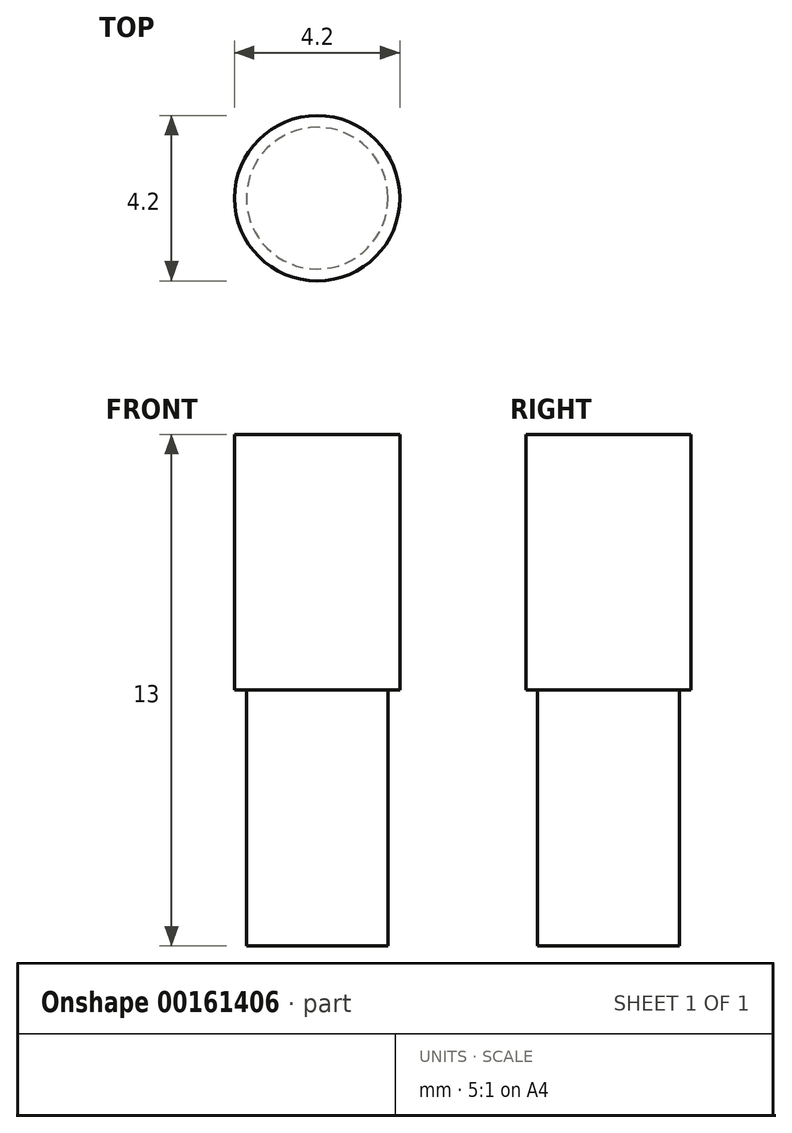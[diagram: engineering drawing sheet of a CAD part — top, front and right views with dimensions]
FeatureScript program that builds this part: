
annotation { "Feature Type Name" : "Feature", "Feature Type Description" : "" }
export const myFeature = defineFeature(function(context is Context, id is Id, definition is map)
    precondition{}
    {
        {
            var Q0;
            Q0=qCreatedBy(makeId("Top.planeOp"),FACE);
            var sketch = newSketch(context, id + "F0", { "sketchPlane" : qUnion([Q0])});
            skCircle(sketch, "E0", {"center": v(0, 0) * mm, "radius": 2.1 * mm});
            skSolve(sketch);
        }
        {
            var Q0;
            Q0=qSketchRegion(id+"F0",true);
            extrude(context, id + "F1", {"entities" : qUnion([Q0]), "oppositeDirection" : true, "depth" : 6.5 * mm});
        }
        {
            var Q0;
            Q0=makeQuery(id+"F1.opExtrude","CAP_FACE",FACE,{"disambiguationData":[OSD([sQuery(id+"F0.wireOp",EDGE,"E0")])],"isStart":false});
            var sketch = newSketch(context, id + "F2", { "sketchPlane" : qUnion([Q0])});
            skCircle(sketch, "E1", {"center": v(0, 0) * mm, "radius": 1.8 * mm});
            skSolve(sketch);
        }
        {
            var Q0;
            Q0=qSketchRegion(id+"F2",true);
            extrude(context, id + "F3", {"entities" : qUnion([Q0]), "operationType" : NewBodyOperationType.ADD, "depth" : 6.5 * mm});
        }
    });
